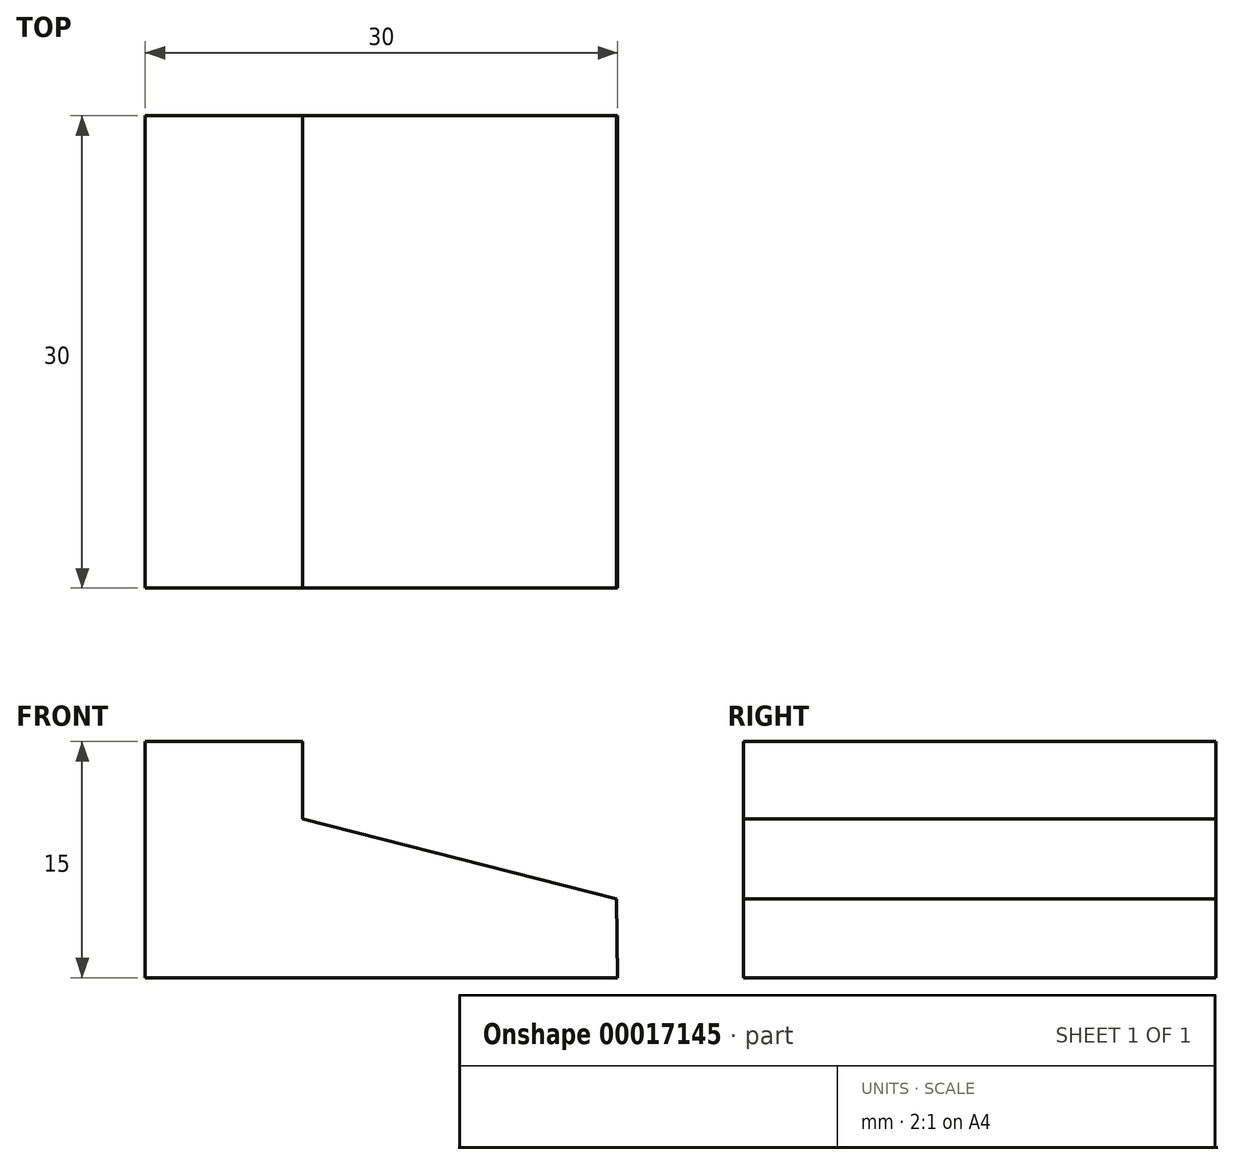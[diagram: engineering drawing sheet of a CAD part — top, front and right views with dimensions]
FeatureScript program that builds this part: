
annotation { "Feature Type Name" : "Feature", "Feature Type Description" : "" }
export const myFeature = defineFeature(function(context is Context, id is Id, definition is map)
    precondition{}
    {
        {
            var Q0;
            Q0=qCreatedBy(makeId("Front.planeOp"),FACE);
            var sketch = newSketch(context, id + "F0", { "sketchPlane" : qUnion([Q0])});
            skLineSegment(sketch, "E0", {"start": v(-15, -5.04) * mm, "end": v(15, -5.04) * mm});
            skLineSegment(sketch, "E1", {"start": v(-15, -5.04) * mm, "end": v(-15, 9.96) * mm});
            skLineSegment(sketch, "E2", {"start": v(-15, 9.96) * mm, "end": v(-5, 9.96) * mm});
            skLineSegment(sketch, "E3", {"start": v(-5, 9.96) * mm, "end": v(-5, 5.04) * mm});
            skLineSegment(sketch, "E4", {"start": v(-5, 5.04) * mm, "end": v(14.94, -0.04) * mm});
            skLineSegment(sketch, "E5", {"start": v(14.94, -0.04) * mm, "end": v(15, -5.04) * mm});
            skSolve(sketch);
        }
        {
            var Q0;
            Q0=makeQuery(id+"F0.imprint","IMPRINT",FACE,{"disambiguationData":[TD([[makeQuery(id+"F0.imprint","IMPRINT",EDGE,{"derivedFrom":sQuery(id+"F0.wireOp",EDGE,"E0")}),1.0]])]});
            extrude(context, id + "F1", {"entities" : qUnion([Q0]), "depth" : 30 * mm});
        }
    });
